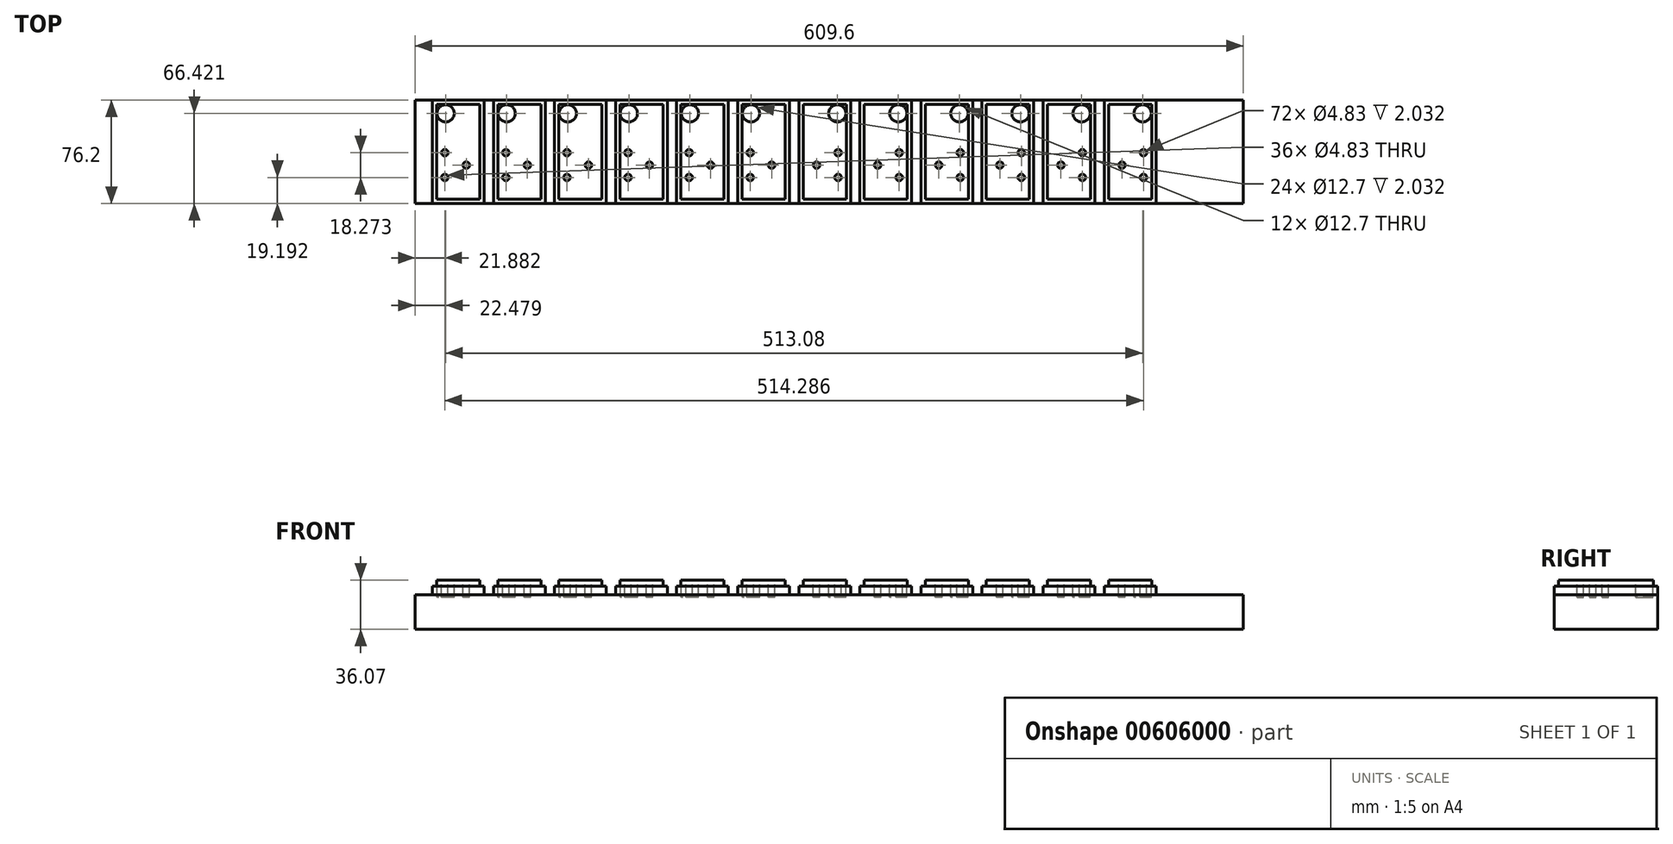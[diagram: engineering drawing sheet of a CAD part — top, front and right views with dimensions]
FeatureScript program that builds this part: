
annotation { "Feature Type Name" : "Feature", "Feature Type Description" : "" }
export const myFeature = defineFeature(function(context is Context, id is Id, definition is map)
    precondition{}
    {
        {
            var Q0;
            Q0=qCreatedBy(makeId("Top.planeOp"),FACE);
            var sketch = newSketch(context, id + "F0", { "sketchPlane" : qUnion([Q0])});
            skLineSegment(sketch, "E0.bottom", {"start": v(0, 0) * mm, "end": v(609.6, 0) * mm});
            skLineSegment(sketch, "E0.top", {"start": v(0, 76.2) * mm, "end": v(609.6, 76.2) * mm});
            skLineSegment(sketch, "E0.left", {"start": v(0, 0) * mm, "end": v(0, 76.2) * mm});
            skLineSegment(sketch, "E0.right", {"start": v(609.6, 0) * mm, "end": v(609.6, 76.2) * mm});
            skSolve(sketch);
        }
        {
            var Q0;
            Q0=makeQuery(id+"F0.imprint","IMPRINT",FACE,{"disambiguationData":[TD([[makeQuery(id+"F0.imprint","IMPRINT",EDGE,{"derivedFrom":sQuery(id+"F0.wireOp",EDGE,"E0.bottom")}),1.0]])]});
            var sketch = newSketch(context, id + "F1", { "sketchPlane" : qUnion([Q0])});
            skLineSegment(sketch, "E1.bottom", {"start": v(12.7, 76.2) * mm, "end": v(50.8, 76.2) * mm});
            skLineSegment(sketch, "E1.top", {"start": v(12.7, 0) * mm, "end": v(50.8, 0) * mm});
            skLineSegment(sketch, "E1.left", {"start": v(12.7, 76.2) * mm, "end": v(12.7, 0) * mm});
            skLineSegment(sketch, "E1.right", {"start": v(50.8, 76.2) * mm, "end": v(50.8, 0) * mm});
            skLineSegment(sketch, "E2.1.0.0", {"start": v(57.66, 76.2) * mm, "end": v(95.76, 76.2) * mm});
            skLineSegment(sketch, "E2.1.0.1", {"start": v(57.66, 76.2) * mm, "end": v(57.66, 0) * mm});
            skLineSegment(sketch, "E2.1.0.2", {"start": v(57.66, 0) * mm, "end": v(95.76, 0) * mm});
            skLineSegment(sketch, "E2.1.0.3", {"start": v(95.76, 76.2) * mm, "end": v(95.76, 0) * mm});
            skLineSegment(sketch, "E2.2.0.0", {"start": v(102.62, 76.2) * mm, "end": v(140.72, 76.2) * mm});
            skLineSegment(sketch, "E2.2.0.1", {"start": v(102.62, 76.2) * mm, "end": v(102.62, 0) * mm});
            skLineSegment(sketch, "E2.2.0.2", {"start": v(102.62, 0) * mm, "end": v(140.72, 0) * mm});
            skLineSegment(sketch, "E2.2.0.3", {"start": v(140.72, 76.2) * mm, "end": v(140.72, 0) * mm});
            skLineSegment(sketch, "E2.3.0.0", {"start": v(147.57, 76.2) * mm, "end": v(185.67, 76.2) * mm});
            skLineSegment(sketch, "E2.3.0.1", {"start": v(147.57, 76.2) * mm, "end": v(147.57, 0) * mm});
            skLineSegment(sketch, "E2.3.0.2", {"start": v(147.57, 0) * mm, "end": v(185.67, 0) * mm});
            skLineSegment(sketch, "E2.3.0.3", {"start": v(185.67, 76.2) * mm, "end": v(185.67, 0) * mm});
            skLineSegment(sketch, "E2.4.0.0", {"start": v(192.53, 76.2) * mm, "end": v(230.63, 76.2) * mm});
            skLineSegment(sketch, "E2.4.0.1", {"start": v(192.53, 76.2) * mm, "end": v(192.53, 0) * mm});
            skLineSegment(sketch, "E2.4.0.2", {"start": v(192.53, 0) * mm, "end": v(230.63, 0) * mm});
            skLineSegment(sketch, "E2.4.0.3", {"start": v(230.63, 76.2) * mm, "end": v(230.63, 0) * mm});
            skLineSegment(sketch, "E2.5.0.0", {"start": v(237.5, 76.2) * mm, "end": v(275.6, 76.2) * mm});
            skLineSegment(sketch, "E2.5.0.1", {"start": v(237.5, 76.2) * mm, "end": v(237.5, 0) * mm});
            skLineSegment(sketch, "E2.5.0.2", {"start": v(237.5, 0) * mm, "end": v(275.6, 0) * mm});
            skLineSegment(sketch, "E2.5.0.3", {"start": v(275.6, 76.2) * mm, "end": v(275.6, 0) * mm});
            skLineSegment(sketch, "E2.6.0.0", {"start": v(282.45, 76.2) * mm, "end": v(320.55, 76.2) * mm});
            skLineSegment(sketch, "E2.6.0.1", {"start": v(282.45, 76.2) * mm, "end": v(282.45, 0) * mm});
            skLineSegment(sketch, "E2.6.0.2", {"start": v(282.45, 0) * mm, "end": v(320.55, 0) * mm});
            skLineSegment(sketch, "E2.6.0.3", {"start": v(320.55, 76.2) * mm, "end": v(320.55, 0) * mm});
            skLineSegment(sketch, "E2.7.0.0", {"start": v(327.4, 76.2) * mm, "end": v(365.5, 76.2) * mm});
            skLineSegment(sketch, "E2.7.0.1", {"start": v(327.4, 76.2) * mm, "end": v(327.4, 0) * mm});
            skLineSegment(sketch, "E2.7.0.2", {"start": v(327.4, 0) * mm, "end": v(365.5, 0) * mm});
            skLineSegment(sketch, "E2.7.0.3", {"start": v(365.5, 76.2) * mm, "end": v(365.5, 0) * mm});
            skLineSegment(sketch, "E2.8.0.0", {"start": v(372.36, 76.2) * mm, "end": v(410.46, 76.2) * mm});
            skLineSegment(sketch, "E2.8.0.1", {"start": v(372.36, 76.2) * mm, "end": v(372.36, 0) * mm});
            skLineSegment(sketch, "E2.8.0.2", {"start": v(372.36, 0) * mm, "end": v(410.46, 0) * mm});
            skLineSegment(sketch, "E2.8.0.3", {"start": v(410.46, 76.2) * mm, "end": v(410.46, 0) * mm});
            skLineSegment(sketch, "E2.9.0.0", {"start": v(417.32, 76.2) * mm, "end": v(455.42, 76.2) * mm});
            skLineSegment(sketch, "E2.9.0.1", {"start": v(417.32, 76.2) * mm, "end": v(417.32, 0) * mm});
            skLineSegment(sketch, "E2.9.0.2", {"start": v(417.32, 0) * mm, "end": v(455.42, 0) * mm});
            skLineSegment(sketch, "E2.9.0.3", {"start": v(455.42, 76.2) * mm, "end": v(455.42, 0) * mm});
            skLineSegment(sketch, "E2.10.0.0", {"start": v(462.28, 76.2) * mm, "end": v(500.38, 76.2) * mm});
            skLineSegment(sketch, "E2.10.0.1", {"start": v(462.28, 76.2) * mm, "end": v(462.28, 0) * mm});
            skLineSegment(sketch, "E2.10.0.2", {"start": v(462.28, 0) * mm, "end": v(500.38, 0) * mm});
            skLineSegment(sketch, "E2.10.0.3", {"start": v(500.38, 76.2) * mm, "end": v(500.38, 0) * mm});
            skLineSegment(sketch, "E2.11.0.0", {"start": v(507.24, 76.2) * mm, "end": v(545.34, 76.2) * mm});
            skLineSegment(sketch, "E2.11.0.1", {"start": v(507.24, 76.2) * mm, "end": v(507.24, 0) * mm});
            skLineSegment(sketch, "E2.11.0.2", {"start": v(507.24, 0) * mm, "end": v(545.34, 0) * mm});
            skLineSegment(sketch, "E2.11.0.3", {"start": v(545.34, 76.2) * mm, "end": v(545.34, 0) * mm});
            skLineSegment(sketch, "E2.direction1", {"start": v(12.7, 76.2) * mm, "end": v(57.66, 76.2) * mm, "construction": true});
            skSolve(sketch);
        }
        {
            var Q0;
            Q0 = qSketchRegion(id + "F1", true);
            extrude(context, id + "F2", {"entities" : qUnion([Q0]), "depth" : 6.35 * mm, "offsetDistance" : 25.4 * mm});
        }
        {
            var Q0;
            Q0=makeQuery(id+"F0.imprint","IMPRINT",FACE,{"disambiguationData":[TD([[makeQuery(id+"F0.imprint","IMPRINT",EDGE,{"derivedFrom":sQuery(id+"F0.wireOp",EDGE,"E0.bottom")}),1.0]])]});
            extrude(context, id + "F3", {"entities" : qUnion([Q0]), "oppositeDirection" : true, "depth" : 25.4 * mm, "offsetDistance" : 25.4 * mm});
        }
        {
            var Q0;
            Q0=makeQuery(id+"F2.opExtrude","CAP_FACE",FACE,{"disambiguationData":[OSD([sQuery(id+"F1.wireOp",EDGE,"E1.bottom"),sQuery(id+"F1.wireOp",EDGE,"E1.top"),sQuery(id+"F1.wireOp",EDGE,"E1.left"),sQuery(id+"F1.wireOp",EDGE,"E1.right")])],"isStart":false});
            var sketch = newSketch(context, id + "F4", { "sketchPlane" : qUnion([Q0])});
            skLineSegment(sketch, "E3.0", {"start": v(47.62, 3.17) * mm, "end": v(47.62, 73.03) * mm});
            skLineSegment(sketch, "E3.1", {"start": v(15.88, 3.17) * mm, "end": v(47.62, 3.17) * mm});
            skLineSegment(sketch, "E3.2", {"start": v(15.87, 73.03) * mm, "end": v(15.88, 3.17) * mm});
            skLineSegment(sketch, "E3.3", {"start": v(47.62, 73.03) * mm, "end": v(15.87, 73.03) * mm});
            skLineSegment(sketch, "E4.0", {"start": v(92.58, 3.17) * mm, "end": v(92.58, 73.03) * mm});
            skLineSegment(sketch, "E4.1", {"start": v(60.83, 3.17) * mm, "end": v(92.58, 3.17) * mm});
            skLineSegment(sketch, "E4.2", {"start": v(60.83, 73.03) * mm, "end": v(60.83, 3.17) * mm});
            skLineSegment(sketch, "E4.3", {"start": v(92.58, 73.03) * mm, "end": v(60.83, 73.03) * mm});
            skLineSegment(sketch, "E5.0", {"start": v(137.54, 3.18) * mm, "end": v(137.54, 73.02) * mm});
            skLineSegment(sketch, "E5.1", {"start": v(105.8, 3.18) * mm, "end": v(137.54, 3.18) * mm});
            skLineSegment(sketch, "E5.2", {"start": v(105.8, 73.02) * mm, "end": v(105.8, 3.18) * mm});
            skLineSegment(sketch, "E5.3", {"start": v(137.54, 73.02) * mm, "end": v(105.8, 73.02) * mm});
            skLineSegment(sketch, "E6.0", {"start": v(182.5, 3.18) * mm, "end": v(182.5, 73.02) * mm});
            skLineSegment(sketch, "E6.1", {"start": v(150.75, 3.18) * mm, "end": v(182.5, 3.18) * mm});
            skLineSegment(sketch, "E6.2", {"start": v(150.75, 73.02) * mm, "end": v(150.75, 3.18) * mm});
            skLineSegment(sketch, "E6.3", {"start": v(182.5, 73.02) * mm, "end": v(150.75, 73.02) * mm});
            skLineSegment(sketch, "E7.0", {"start": v(227.46, 3.18) * mm, "end": v(227.46, 73.02) * mm});
            skLineSegment(sketch, "E7.1", {"start": v(195.7, 3.18) * mm, "end": v(227.46, 3.18) * mm});
            skLineSegment(sketch, "E7.2", {"start": v(195.7, 73.02) * mm, "end": v(195.7, 3.18) * mm});
            skLineSegment(sketch, "E7.3", {"start": v(227.46, 73.02) * mm, "end": v(195.7, 73.02) * mm});
            skLineSegment(sketch, "E8.0", {"start": v(272.42, 3.17) * mm, "end": v(272.42, 73.03) * mm});
            skLineSegment(sketch, "E8.1", {"start": v(240.67, 3.17) * mm, "end": v(272.42, 3.17) * mm});
            skLineSegment(sketch, "E8.2", {"start": v(240.67, 73.03) * mm, "end": v(240.67, 3.17) * mm});
            skLineSegment(sketch, "E8.3", {"start": v(272.42, 73.03) * mm, "end": v(240.67, 73.03) * mm});
            skLineSegment(sketch, "E9.0", {"start": v(317.37, 3.17) * mm, "end": v(317.37, 73.03) * mm});
            skLineSegment(sketch, "E9.1", {"start": v(285.62, 3.17) * mm, "end": v(317.37, 3.17) * mm});
            skLineSegment(sketch, "E9.2", {"start": v(285.62, 73.03) * mm, "end": v(285.62, 3.17) * mm});
            skLineSegment(sketch, "E9.3", {"start": v(317.37, 73.03) * mm, "end": v(285.62, 73.03) * mm});
            skLineSegment(sketch, "E10.0", {"start": v(362.33, 3.17) * mm, "end": v(362.33, 73.03) * mm});
            skLineSegment(sketch, "E10.1", {"start": v(330.58, 3.17) * mm, "end": v(362.33, 3.17) * mm});
            skLineSegment(sketch, "E10.2", {"start": v(330.58, 73.03) * mm, "end": v(330.58, 3.17) * mm});
            skLineSegment(sketch, "E10.3", {"start": v(362.33, 73.03) * mm, "end": v(330.58, 73.03) * mm});
            skLineSegment(sketch, "E11.0", {"start": v(407.29, 3.17) * mm, "end": v(407.29, 73.03) * mm});
            skLineSegment(sketch, "E11.1", {"start": v(375.54, 3.17) * mm, "end": v(407.29, 3.17) * mm});
            skLineSegment(sketch, "E11.2", {"start": v(375.54, 73.03) * mm, "end": v(375.54, 3.17) * mm});
            skLineSegment(sketch, "E11.3", {"start": v(407.29, 73.03) * mm, "end": v(375.54, 73.03) * mm});
            skLineSegment(sketch, "E12.0", {"start": v(452.25, 3.17) * mm, "end": v(452.25, 73.03) * mm});
            skLineSegment(sketch, "E12.1", {"start": v(420.5, 3.17) * mm, "end": v(452.25, 3.17) * mm});
            skLineSegment(sketch, "E12.2", {"start": v(420.5, 73.03) * mm, "end": v(420.5, 3.17) * mm});
            skLineSegment(sketch, "E12.3", {"start": v(452.25, 73.03) * mm, "end": v(420.5, 73.03) * mm});
            skLineSegment(sketch, "E13.0", {"start": v(497.2, 3.17) * mm, "end": v(497.2, 73.03) * mm});
            skLineSegment(sketch, "E13.1", {"start": v(465.46, 3.17) * mm, "end": v(497.2, 3.17) * mm});
            skLineSegment(sketch, "E13.2", {"start": v(465.46, 73.03) * mm, "end": v(465.46, 3.17) * mm});
            skLineSegment(sketch, "E13.3", {"start": v(497.2, 73.03) * mm, "end": v(465.46, 73.03) * mm});
            skLineSegment(sketch, "E14.0", {"start": v(542.16, 3.18) * mm, "end": v(542.16, 73.02) * mm});
            skLineSegment(sketch, "E14.1", {"start": v(510.41, 3.18) * mm, "end": v(542.16, 3.18) * mm});
            skLineSegment(sketch, "E14.2", {"start": v(510.41, 73.02) * mm, "end": v(510.41, 3.18) * mm});
            skLineSegment(sketch, "E14.3", {"start": v(542.16, 73.02) * mm, "end": v(510.41, 73.02) * mm});
            skSolve(sketch);
        }
        {
            var Q0;
            Q0=makeQuery(id+"F4.imprint","IMPRINT",FACE,{"disambiguationData":[TD([[makeQuery(id+"F4.imprint","IMPRINT",EDGE,{"derivedFrom":sQuery(id+"F4.wireOp",EDGE,"E3.0")}),1.0]])]});
            var Q1;
            Q1=makeQuery(id+"F4.imprint","IMPRINT",FACE,{"disambiguationData":[TD([[makeQuery(id+"F4.imprint","IMPRINT",EDGE,{"derivedFrom":sQuery(id+"F4.wireOp",EDGE,"E4.0")}),1.0]])]});
            var Q2;
            Q2=makeQuery(id+"F4.imprint","IMPRINT",FACE,{"disambiguationData":[TD([[makeQuery(id+"F4.imprint","IMPRINT",EDGE,{"derivedFrom":sQuery(id+"F4.wireOp",EDGE,"E5.0")}),1.0]])]});
            var Q3;
            Q3=makeQuery(id+"F4.imprint","IMPRINT",FACE,{"disambiguationData":[TD([[makeQuery(id+"F4.imprint","IMPRINT",EDGE,{"derivedFrom":sQuery(id+"F4.wireOp",EDGE,"E6.0")}),1.0]])]});
            var Q4;
            Q4=makeQuery(id+"F4.imprint","IMPRINT",FACE,{"disambiguationData":[TD([[makeQuery(id+"F4.imprint","IMPRINT",EDGE,{"derivedFrom":sQuery(id+"F4.wireOp",EDGE,"E7.0")}),1.0]])]});
            var Q5;
            Q5=makeQuery(id+"F4.imprint","IMPRINT",FACE,{"disambiguationData":[TD([[makeQuery(id+"F4.imprint","IMPRINT",EDGE,{"derivedFrom":sQuery(id+"F4.wireOp",EDGE,"E8.0")}),1.0]])]});
            var Q6;
            Q6=makeQuery(id+"F4.imprint","IMPRINT",FACE,{"disambiguationData":[TD([[makeQuery(id+"F4.imprint","IMPRINT",EDGE,{"derivedFrom":sQuery(id+"F4.wireOp",EDGE,"E9.0")}),1.0]])]});
            var Q7;
            Q7=makeQuery(id+"F4.imprint","IMPRINT",FACE,{"disambiguationData":[TD([[makeQuery(id+"F4.imprint","IMPRINT",EDGE,{"derivedFrom":sQuery(id+"F4.wireOp",EDGE,"E10.0")}),1.0]])]});
            var Q8;
            Q8=makeQuery(id+"F4.imprint","IMPRINT",FACE,{"disambiguationData":[TD([[makeQuery(id+"F4.imprint","IMPRINT",EDGE,{"derivedFrom":sQuery(id+"F4.wireOp",EDGE,"E11.0")}),1.0]])]});
            var Q9;
            Q9=makeQuery(id+"F4.imprint","IMPRINT",FACE,{"disambiguationData":[TD([[makeQuery(id+"F4.imprint","IMPRINT",EDGE,{"derivedFrom":sQuery(id+"F4.wireOp",EDGE,"E12.0")}),1.0]])]});
            var Q10;
            Q10=makeQuery(id+"F4.imprint","IMPRINT",FACE,{"disambiguationData":[TD([[makeQuery(id+"F4.imprint","IMPRINT",EDGE,{"derivedFrom":sQuery(id+"F4.wireOp",EDGE,"E13.0")}),1.0]])]});
            var Q11;
            Q11=makeQuery(id+"F4.imprint","IMPRINT",FACE,{"disambiguationData":[TD([[makeQuery(id+"F4.imprint","IMPRINT",EDGE,{"derivedFrom":sQuery(id+"F4.wireOp",EDGE,"E14.0")}),1.0]])]});
            extrude(context, id + "F5", {"entities" : qUnion([Q0, Q1, Q2, Q3, Q4, Q5, Q6, Q7, Q8, Q9, Q10, Q11]), "operationType" : NewBodyOperationType.ADD, "depth" : 4.32 * mm, "offsetDistance" : 25.4 * mm});
        }
        {
            var Q0;
            Q0=makeQuery(id+"F5.opExtrude","CAP_FACE",FACE,{"disambiguationData":[OSD([sQuery(id+"F4.wireOp",EDGE,"E3.0"),sQuery(id+"F4.wireOp",EDGE,"E3.1"),sQuery(id+"F4.wireOp",EDGE,"E3.2"),sQuery(id+"F4.wireOp",EDGE,"E3.3")])],"isStart":false});
            var sketch = newSketch(context, id + "F6", { "sketchPlane" : qUnion([Q0])});
            skCircle(sketch, "E15", {"center": v(22.48, 66.42) * mm, "radius": 6.35 * mm});
            skCircle(sketch, "E16.1.0.0", {"center": v(67.44, 66.42) * mm, "radius": 6.35 * mm});
            skCircle(sketch, "E16.2.0.0", {"center": v(112.4, 66.42) * mm, "radius": 6.35 * mm});
            skCircle(sketch, "E16.3.0.0", {"center": v(157.35, 66.42) * mm, "radius": 6.35 * mm});
            skCircle(sketch, "E16.4.0.0", {"center": v(202.31, 66.42) * mm, "radius": 6.35 * mm});
            skCircle(sketch, "E16.5.0.0", {"center": v(247.27, 66.42) * mm, "radius": 6.35 * mm});
            skLineSegment(sketch, "E16.direction1", {"start": v(22.48, 66.42) * mm, "end": v(67.44, 66.42) * mm, "construction": true});
            skCircle(sketch, "E17", {"center": v(310.77, 66.42) * mm, "radius": 6.35 * mm});
            skCircle(sketch, "E18.1.0.0", {"center": v(355.73, 66.42) * mm, "radius": 6.35 * mm});
            skCircle(sketch, "E18.2.0.0", {"center": v(400.69, 66.42) * mm, "radius": 6.35 * mm});
            skCircle(sketch, "E18.3.0.0", {"center": v(445.64, 66.42) * mm, "radius": 6.35 * mm});
            skCircle(sketch, "E18.4.0.0", {"center": v(490.6, 66.42) * mm, "radius": 6.35 * mm});
            skCircle(sketch, "E18.5.0.0", {"center": v(535.56, 66.42) * mm, "radius": 6.35 * mm});
            skLineSegment(sketch, "E18.direction1", {"start": v(310.77, 66.42) * mm, "end": v(355.73, 66.42) * mm, "construction": true});
            skCircle(sketch, "E19", {"center": v(27.15, 28.32) * mm, "radius": 14.45 * mm, "construction": true});
            skCircle(sketch, "E20", {"center": v(21.88, 37.45) * mm, "radius": 2.41 * mm});
            skCircle(sketch, "E21.1.0", {"center": v(21.88, 19.2) * mm, "radius": 2.41 * mm});
            skCircle(sketch, "E21.2.0", {"center": v(37.7, 28.32) * mm, "radius": 2.41 * mm});
            skLineSegment(sketch, "E22", {"start": v(21.88, 37.45) * mm, "end": v(21.88, 19.2) * mm, "construction": true});
            skCircle(sketch, "E23.1.0.0", {"center": v(66.84, 37.45) * mm, "radius": 2.41 * mm});
            skCircle(sketch, "E23.1.0.1", {"center": v(82.65, 28.32) * mm, "radius": 2.41 * mm});
            skCircle(sketch, "E23.1.0.2", {"center": v(66.84, 19.2) * mm, "radius": 2.41 * mm});
            skCircle(sketch, "E23.2.0.0", {"center": v(111.8, 37.45) * mm, "radius": 2.41 * mm});
            skCircle(sketch, "E23.2.0.1", {"center": v(127.6, 28.32) * mm, "radius": 2.41 * mm});
            skCircle(sketch, "E23.2.0.2", {"center": v(111.8, 19.2) * mm, "radius": 2.41 * mm});
            skCircle(sketch, "E23.3.0.0", {"center": v(156.76, 37.45) * mm, "radius": 2.41 * mm});
            skCircle(sketch, "E23.3.0.1", {"center": v(172.57, 28.32) * mm, "radius": 2.41 * mm});
            skCircle(sketch, "E23.3.0.2", {"center": v(156.76, 19.2) * mm, "radius": 2.41 * mm});
            skCircle(sketch, "E23.4.0.0", {"center": v(201.71, 37.45) * mm, "radius": 2.41 * mm});
            skCircle(sketch, "E23.4.0.1", {"center": v(217.53, 28.32) * mm, "radius": 2.41 * mm});
            skCircle(sketch, "E23.4.0.2", {"center": v(201.71, 19.2) * mm, "radius": 2.41 * mm});
            skCircle(sketch, "E23.5.0.0", {"center": v(246.67, 37.45) * mm, "radius": 2.41 * mm});
            skCircle(sketch, "E23.5.0.1", {"center": v(262.48, 28.32) * mm, "radius": 2.41 * mm});
            skCircle(sketch, "E23.5.0.2", {"center": v(246.67, 19.2) * mm, "radius": 2.41 * mm});
            skLineSegment(sketch, "E23.direction1", {"start": v(21.88, 37.45) * mm, "end": v(66.84, 37.45) * mm, "construction": true});
            skCircle(sketch, "E24", {"center": v(311.38, 37.47) * mm, "radius": 2.41 * mm});
            skCircle(sketch, "E25", {"center": v(311.38, 19.2) * mm, "radius": 2.41 * mm});
            skCircle(sketch, "E26", {"center": v(295.56, 28.33) * mm, "radius": 2.41 * mm});
            skLineSegment(sketch, "E27", {"start": v(295.56, 28.33) * mm, "end": v(311.38, 37.47) * mm, "construction": true});
            skLineSegment(sketch, "E28", {"start": v(311.38, 37.47) * mm, "end": v(311.38, 19.2) * mm, "construction": true});
            skLineSegment(sketch, "E29", {"start": v(311.38, 19.2) * mm, "end": v(295.56, 28.33) * mm, "construction": true});
            skCircle(sketch, "E30.1.0.0", {"center": v(340.52, 28.33) * mm, "radius": 2.41 * mm});
            skCircle(sketch, "E30.1.0.1", {"center": v(356.34, 19.2) * mm, "radius": 2.41 * mm});
            skCircle(sketch, "E30.1.0.2", {"center": v(356.34, 37.47) * mm, "radius": 2.41 * mm});
            skCircle(sketch, "E30.2.0.0", {"center": v(385.48, 28.33) * mm, "radius": 2.41 * mm});
            skCircle(sketch, "E30.2.0.1", {"center": v(401.3, 19.2) * mm, "radius": 2.41 * mm});
            skCircle(sketch, "E30.2.0.2", {"center": v(401.3, 37.47) * mm, "radius": 2.41 * mm});
            skCircle(sketch, "E30.3.0.0", {"center": v(430.44, 28.33) * mm, "radius": 2.41 * mm});
            skCircle(sketch, "E30.3.0.1", {"center": v(446.25, 19.2) * mm, "radius": 2.41 * mm});
            skCircle(sketch, "E30.3.0.2", {"center": v(446.25, 37.47) * mm, "radius": 2.41 * mm});
            skCircle(sketch, "E30.4.0.0", {"center": v(475.4, 28.33) * mm, "radius": 2.41 * mm});
            skCircle(sketch, "E30.4.0.1", {"center": v(491.21, 19.2) * mm, "radius": 2.41 * mm});
            skCircle(sketch, "E30.4.0.2", {"center": v(491.21, 37.47) * mm, "radius": 2.41 * mm});
            skCircle(sketch, "E30.5.0.0", {"center": v(520.35, 28.33) * mm, "radius": 2.41 * mm});
            skCircle(sketch, "E30.5.0.1", {"center": v(536.17, 19.2) * mm, "radius": 2.41 * mm});
            skCircle(sketch, "E30.5.0.2", {"center": v(536.17, 37.47) * mm, "radius": 2.41 * mm});
            skLineSegment(sketch, "E30.direction1", {"start": v(295.56, 28.33) * mm, "end": v(340.52, 28.33) * mm, "construction": true});
            skSolve(sketch);
        }
        {
            var Q0;
            Q0 = qSketchRegion(id + "F6", true);
            extrude(context, id + "F7", {"entities" : qUnion([Q0]), "operationType" : NewBodyOperationType.REMOVE, "oppositeDirection" : true, "depth" : 12.7 * mm, "offsetDistance" : 25.4 * mm});
        }
    });
